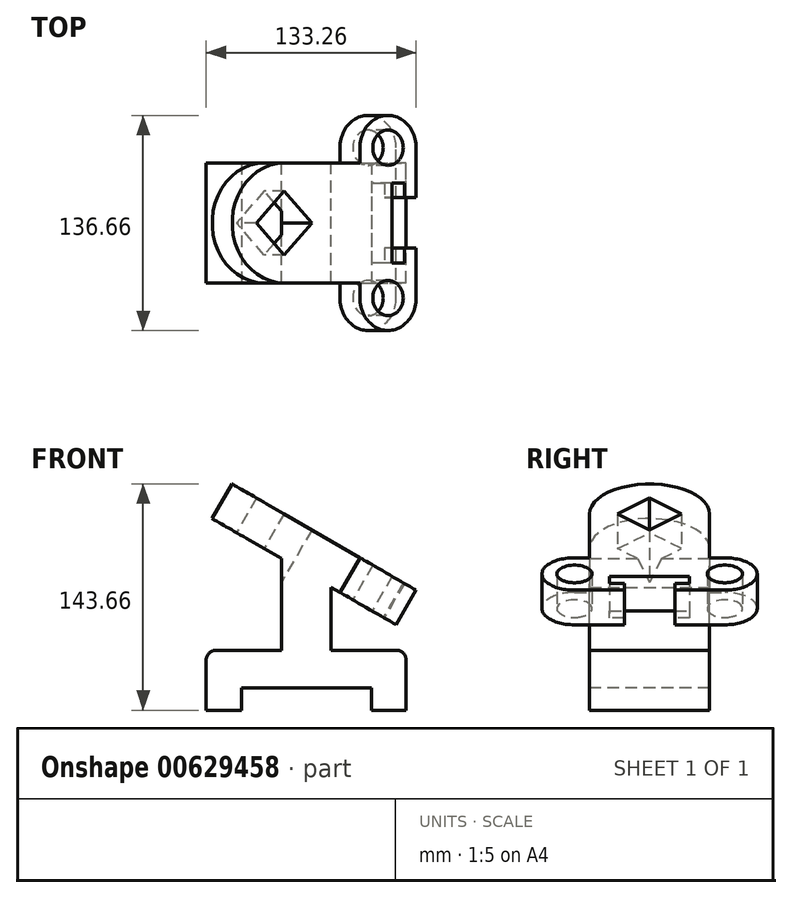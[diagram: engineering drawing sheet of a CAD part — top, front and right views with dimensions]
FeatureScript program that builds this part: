
annotation { "Feature Type Name" : "Feature", "Feature Type Description" : "" }
export const myFeature = defineFeature(function(context is Context, id is Id, definition is map)
    precondition{}
    {
        {
            var Q0;
            Q0=qCreatedBy(makeId("Front.planeOp"),FACE);
            var sketch = newSketch(context, id + "F0", { "sketchPlane" : qUnion([Q0])});
            skLineSegment(sketch, "E0.bottom", {"start": v(-63.5, 38.1) * mm, "end": v(63.5, 38.1) * mm});
            skLineSegment(sketch, "E0.top", {"start": v(-63.5, 0) * mm, "end": v(63.5, 0) * mm});
            skLineSegment(sketch, "E0.left", {"start": v(-63.5, 38.1) * mm, "end": v(-63.5, 0) * mm});
            skLineSegment(sketch, "E0.right", {"start": v(63.5, 38.1) * mm, "end": v(63.5, 0) * mm});
            skPoint(sketch, "E1", {"position": v(0, 0) * mm});
            skSolve(sketch);
        }
        {
            var Q0;
            Q0=makeQuery(id+"F0.imprint","IMPRINT",FACE,{"disambiguationData":[TD([[makeQuery(id+"F0.imprint","IMPRINT",EDGE,{"derivedFrom":sQuery(id+"F0.wireOp",EDGE,"E0.bottom")}),-1.0]])]});
            extrude(context, id + "F1", {"entities" : qUnion([Q0]), "depth" : 76.2 * mm, "offsetDistance" : 25.4 * mm, "symmetric" : true});
        }
        {
            var Q0;
            Q0=qCreatedBy(makeId("Front.planeOp"),FACE);
            var sketch = newSketch(context, id + "F2", { "sketchPlane" : qUnion([Q0])});
            skLineSegment(sketch, "E2", {"start": v(-41.15, 0) * mm, "end": v(-41.15, 14.22) * mm});
            skLineSegment(sketch, "E3", {"start": v(-41.15, 14.22) * mm, "end": v(41.4, 14.22) * mm});
            skLineSegment(sketch, "E4", {"start": v(41.4, 14.22) * mm, "end": v(41.4, 0) * mm});
            skLineSegment(sketch, "E5", {"start": v(-41.15, 0) * mm, "end": v(41.4, 0) * mm});
            skSolve(sketch);
        }
        {
            var Q0;
            Q0=makeQuery(id+"F2.imprint","IMPRINT",FACE,{"disambiguationData":[TD([[makeQuery(id+"F2.imprint","IMPRINT",EDGE,{"derivedFrom":sQuery(id+"F2.wireOp",EDGE,"E2")}),-1.0]])]});
            extrude(context, id + "F3", {"entities" : qUnion([Q0]), "operationType" : NewBodyOperationType.REMOVE, "endBound" : BoundingType.THROUGH_ALL, "oppositeDirection" : true, "depth" : 83.31 * mm, "offsetDistance" : 25.4 * mm, "hasSecondDirection" : true, "secondDirectionBound" : BoundingType.THROUGH_ALL, "secondDirectionOppositeDirection" : false, "secondDirectionDepth" : 25.4 * mm});
        }
        {
            var Q0;
            Q0=qCreatedBy(makeId("Front.planeOp"),FACE);
            var sketch = newSketch(context, id + "F4", { "sketchPlane" : qUnion([Q0])});
            skLineSegment(sketch, "E6.bottom", {"start": v(15.75, 38.1) * mm, "end": v(-15.75, 38.1) * mm});
            skLineSegment(sketch, "E6.top", {"start": v(15.75, 96.27) * mm, "end": v(-15.75, 96.27) * mm});
            skLineSegment(sketch, "E6.left", {"start": v(15.75, 38.1) * mm, "end": v(15.75, 96.27) * mm});
            skLineSegment(sketch, "E6.right", {"start": v(-15.75, 38.1) * mm, "end": v(-15.75, 96.27) * mm});
            skPoint(sketch, "E6.middle", {"position": v(0, 67.18) * mm});
            skLineSegment(sketch, "E7.0.0", {"start": v(-63.5, 0) * mm, "end": v(-41.15, 0) * mm, "construction": true});
            skLineSegment(sketch, "E7.0.1", {"start": v(-41.15, 0) * mm, "end": v(-41.15, 14.22) * mm, "construction": true});
            skLineSegment(sketch, "E7.0.2", {"start": v(-41.15, 14.22) * mm, "end": v(41.4, 14.22) * mm, "construction": true});
            skLineSegment(sketch, "E7.0.3", {"start": v(41.4, 14.22) * mm, "end": v(41.4, 0) * mm, "construction": true});
            skLineSegment(sketch, "E7.0.4", {"start": v(41.4, 0) * mm, "end": v(63.5, 0) * mm, "construction": true});
            skLineSegment(sketch, "E7.0.5", {"start": v(63.5, 0) * mm, "end": v(63.5, 38.1) * mm, "construction": true});
            skLineSegment(sketch, "E7.0.7", {"start": v(-63.5, 38.1) * mm, "end": v(-63.5, 0) * mm, "construction": true});
            skLineSegment(sketch, "E8.0.0", {"start": v(63.5, 38.1) * mm, "end": v(-63.5, 38.1) * mm, "construction": true});
            skSolve(sketch);
        }
        {
            var Q0;
            Q0=makeQuery(id+"F4.imprint","IMPRINT",FACE,{"disambiguationData":[TD([[makeQuery(id+"F4.imprint","IMPRINT",EDGE,{"derivedFrom":sQuery(id+"F4.wireOp",EDGE,"E6.bottom")}),-1.0]])]});
            var Q1;
            Q1=makeQuery(id+"F1.opExtrude","CAP_FACE",FACE,{"disambiguationData":[OSD([sQuery(id+"F0.wireOp",EDGE,"E0.bottom"),sQuery(id+"F0.wireOp",EDGE,"E0.top"),sQuery(id+"F0.wireOp",EDGE,"E0.left"),sQuery(id+"F0.wireOp",EDGE,"E0.right")])],"isStart":false});
            var Q2;
            Q2=makeQuery(id+"F1.opExtrude","CAP_FACE",FACE,{"disambiguationData":[OSD([sQuery(id+"F0.wireOp",EDGE,"E0.bottom"),sQuery(id+"F0.wireOp",EDGE,"E0.top"),sQuery(id+"F0.wireOp",EDGE,"E0.left"),sQuery(id+"F0.wireOp",EDGE,"E0.right")])],"isStart":true});
            extrude(context, id + "F5", {"entities" : qUnion([Q0]), "operationType" : NewBodyOperationType.ADD, "endBound" : BoundingType.UP_TO_SURFACE, "depth" : 25.4 * mm, "endBoundEntityFace" : qUnion([Q1]), "offsetDistance" : 25.4 * mm, "hasSecondDirection" : true, "secondDirectionBound" : BoundingType.UP_TO_SURFACE, "secondDirectionOppositeDirection" : true, "secondDirectionDepth" : 25.4 * mm, "secondDirectionBoundEntityFace" : qUnion([Q2])});
        }
        {
            var Q0;
            Q0=makeQuery(id+"F5.opExtrude","SWEPT_FACE",FACE,{"disambiguationData":[OSD([sQuery(id+"F4.wireOp",EDGE,"E6.top")])]});
            var sketch = newSketch(context, id + "F6", { "sketchPlane" : qUnion([Q0])});
            skLineSegment(sketch, "E9", {"start": v(-15.75, -38.1) * mm, "end": v(-15.75, 38.1) * mm});
            skLineSegment(sketch, "E10", {"start": v(28.45, -38.1) * mm, "end": v(-28.45, -38.1) * mm});
            skLineSegment(sketch, "E11", {"start": v(15.75, -38.1) * mm, "end": v(15.75, 38.1) * mm});
            skLineSegment(sketch, "E12", {"start": v(28.45, 38.1) * mm, "end": v(-28.45, 38.1) * mm});
            skSolve(sketch);
        }
        {
            var Q0;
            Q0=sQuery(id+"F6.wireOp",EDGE,"E9");
            cPlane(context, id + "F7", {"entities" : qUnion([Q0]), "cplaneType" : CPlaneType.LINE_ANGLE, "offset" : 25.4 * mm, "angle" : 30 * degree, "width" : 152.4 * mm, "height" : 152.4 * mm});
        }
        {
            var Q0;
            Q0=qCreatedBy(id+"F7.planeOp",FACE);
            var sketch = newSketch(context, id + "F8", { "sketchPlane" : qUnion([Q0])});
            skArc(sketch, "E13", {"start": v(-74.47, 38.1) * mm, "mid": v(-112.57, 0) * mm, "end": v(-74.47, -38.1) * mm});
            skArc(sketch, "E14", {"start": v(22.3, 47.75) * mm, "mid": v(1.73, 68.33) * mm, "end": v(-18.85, 47.75) * mm});
            skArc(sketch, "E15", {"start": v(-18.85, -47.75) * mm, "mid": v(1.73, -68.33) * mm, "end": v(22.3, -47.75) * mm});
            skLineSegment(sketch, "E16", {"start": v(-138.8, 0) * mm, "end": v(16.25, 0) * mm, "construction": true});
            skLineSegment(sketch, "E17", {"start": v(22.3, -47.75) * mm, "end": v(22.3, -16) * mm});
            skLineSegment(sketch, "E18", {"start": v(-18.85, -47.75) * mm, "end": v(-18.85, -38.1) * mm});
            skLineSegment(sketch, "E19", {"start": v(-74.47, 38.1) * mm, "end": v(-18.85, 38.1) * mm});
            skLineSegment(sketch, "E20", {"start": v(-74.47, -38.1) * mm, "end": v(-18.85, -38.1) * mm});
            skLineSegment(sketch, "E21.trimOffspring", {"start": v(-18.85, 38.1) * mm, "end": v(-18.85, 47.75) * mm});
            skCircle(sketch, "E22", {"center": v(1.73, -47.75) * mm, "radius": 11.18 * mm});
            skCircle(sketch, "E23", {"center": v(1.73, 47.75) * mm, "radius": 11.18 * mm});
            skLineSegment(sketch, "E24", {"start": v(22.3, -16) * mm, "end": v(13.67, -16) * mm});
            skLineSegment(sketch, "E25", {"start": v(13.67, -16) * mm, "end": v(13.67, -25.4) * mm});
            skLineSegment(sketch, "E26", {"start": v(13.67, -25.4) * mm, "end": v(4.78, -25.4) * mm});
            skLineSegment(sketch, "E27", {"start": v(4.78, -25.4) * mm, "end": v(4.78, 25.4) * mm});
            skLineSegment(sketch, "E28", {"start": v(4.78, 25.4) * mm, "end": v(13.67, 25.4) * mm});
            skLineSegment(sketch, "E29", {"start": v(13.67, 25.4) * mm, "end": v(13.67, 16) * mm});
            skLineSegment(sketch, "E30", {"start": v(13.67, 16) * mm, "end": v(22.3, 16) * mm});
            skLineSegment(sketch, "E31.bottom", {"start": v(-54.18, 0) * mm, "end": v(-74.47, 20.3) * mm});
            skLineSegment(sketch, "E31.top", {"start": v(-74.47, -20.3) * mm, "end": v(-94.77, 0) * mm});
            skLineSegment(sketch, "E31.left", {"start": v(-54.18, 0) * mm, "end": v(-74.47, -20.3) * mm});
            skLineSegment(sketch, "E31.right", {"start": v(-74.47, 20.3) * mm, "end": v(-94.77, 0) * mm});
            skLineSegment(sketch, "E32.trimOffspring", {"start": v(22.3, 16) * mm, "end": v(22.3, 47.75) * mm});
            skLineSegment(sketch, "E33", {"start": v(5.73, 0) * mm, "end": v(-100.34, 0) * mm, "construction": true});
            skSolve(sketch);
        }
        {
            var Q0;
            Q0=makeQuery(id+"F8.imprint","IMPRINT",FACE,{"disambiguationData":[TD([[makeQuery(id+"F8.imprint","IMPRINT",EDGE,{"derivedFrom":sQuery(id+"F8.wireOp",EDGE,"E13")}),1.0]])]});
            extrude(context, id + "F9", {"entities" : qUnion([Q0]), "operationType" : NewBodyOperationType.ADD, "depth" : 25.4 * mm, "offsetDistance" : 25.4 * mm});
        }
        {
            var Q0;
            Q0=makeQuery(id+"F8.imprint","IMPRINT",FACE,{"disambiguationData":[TD([[makeQuery(id+"F8.imprint","IMPRINT",EDGE,{"derivedFrom":sQuery(id+"F8.wireOp",EDGE,"E31.bottom")}),1.0]])]});
            var Q1;
            {var subQ0=sQuery(id+"F0.wireOp",EDGE,"E0.left");var subQ3=sQuery(id+"F0.wireOp",EDGE,"E0.bottom");Q1=makeQuery(id+"F5.boolean.opBoolean","SPLIT",FACE,{"disambiguationData":[TD([makeQuery(id+"F1.opExtrude","SWEPT_FACE",FACE,{"disambiguationData":[OSD([subQ0])]})])],"derivedFrom":makeQuery(id+"F1.opExtrude","SWEPT_FACE",FACE,{"disambiguationData":[OSD([subQ3])]})});}
            var Q2;
            Q2=makeQuery(id+"F9.opExtrude","CAP_FACE",FACE,{"disambiguationData":[OSD([sQuery(id+"F8.wireOp",EDGE,"E13"),sQuery(id+"F8.wireOp",EDGE,"E14"),sQuery(id+"F8.wireOp",EDGE,"E15"),sQuery(id+"F8.wireOp",EDGE,"E17"),sQuery(id+"F8.wireOp",EDGE,"E18"),sQuery(id+"F8.wireOp",EDGE,"E19"),sQuery(id+"F8.wireOp",EDGE,"E20"),sQuery(id+"F8.wireOp",EDGE,"E21.trimOffspring"),sQuery(id+"F8.wireOp",EDGE,"E22"),sQuery(id+"F8.wireOp",EDGE,"E23"),sQuery(id+"F8.wireOp",EDGE,"E24"),sQuery(id+"F8.wireOp",EDGE,"E25"),sQuery(id+"F8.wireOp",EDGE,"E26"),sQuery(id+"F8.wireOp",EDGE,"E27"),sQuery(id+"F8.wireOp",EDGE,"E28"),sQuery(id+"F8.wireOp",EDGE,"E29"),sQuery(id+"F8.wireOp",EDGE,"E30"),sQuery(id+"F8.wireOp",EDGE,"E31.bottom"),sQuery(id+"F8.wireOp",EDGE,"E31.top"),sQuery(id+"F8.wireOp",EDGE,"E31.left"),sQuery(id+"F8.wireOp",EDGE,"E31.right"),sQuery(id+"F8.wireOp",EDGE,"E32.trimOffspring")])],"isStart":false});
            extrude(context, id + "F10", {"entities" : qUnion([Q0]), "operationType" : NewBodyOperationType.REMOVE, "endBound" : BoundingType.UP_TO_SURFACE, "oppositeDirection" : true, "depth" : 25.4 * mm, "endBoundEntityFace" : qUnion([Q1]), "offsetDistance" : 25.4 * mm, "hasSecondDirection" : true, "secondDirectionBound" : BoundingType.UP_TO_SURFACE, "secondDirectionOppositeDirection" : false, "secondDirectionDepth" : 25.4 * mm, "secondDirectionBoundEntityFace" : qUnion([Q2])});
        }
        {
            var Q0;
            Q0=makeQuery(id+"F1.opExtrude","SWEPT_EDGE",EDGE,{"disambiguationData":[OSD([sQuery(id+"F0.wireOp",EDGE,"E0.bottom"),sQuery(id+"F0.wireOp",EDGE,"E0.right")])]});
            var Q1;
            Q1=makeQuery(id+"F1.opExtrude","SWEPT_EDGE",EDGE,{"disambiguationData":[OSD([sQuery(id+"F0.wireOp",EDGE,"E0.bottom"),sQuery(id+"F0.wireOp",EDGE,"E0.left")])]});
            var Q2;
            Q2=makeQuery(id+"F5.opExtrude","TWEAK_EDGE",EDGE,{"derivedFrom":[makeQuery(id+"F4.imprint","IMPRINT",EDGE,{"derivedFrom":sQuery(id+"F4.wireOp",EDGE,"E6.bottom")}),makeQuery(id+"F4.imprint","IMPRINT",EDGE,{"derivedFrom":sQuery(id+"F4.wireOp",EDGE,"E6.left")})]});
            var Q3;
            Q3=makeQuery(id+"F5.opExtrude","TWEAK_EDGE",EDGE,{"derivedFrom":[makeQuery(id+"F4.imprint","IMPRINT",EDGE,{"derivedFrom":sQuery(id+"F4.wireOp",EDGE,"E6.bottom")}),makeQuery(id+"F4.imprint","IMPRINT",EDGE,{"derivedFrom":sQuery(id+"F4.wireOp",EDGE,"E6.right")})]});
            fillet(context, id + "F11", {"entities" : qUnion([Q0, Q1, Q2, Q3]), "radius" : 6.35 * mm, "tangentPropagation" : true, "allowEdgeOverflow" : false});
        }
    });
